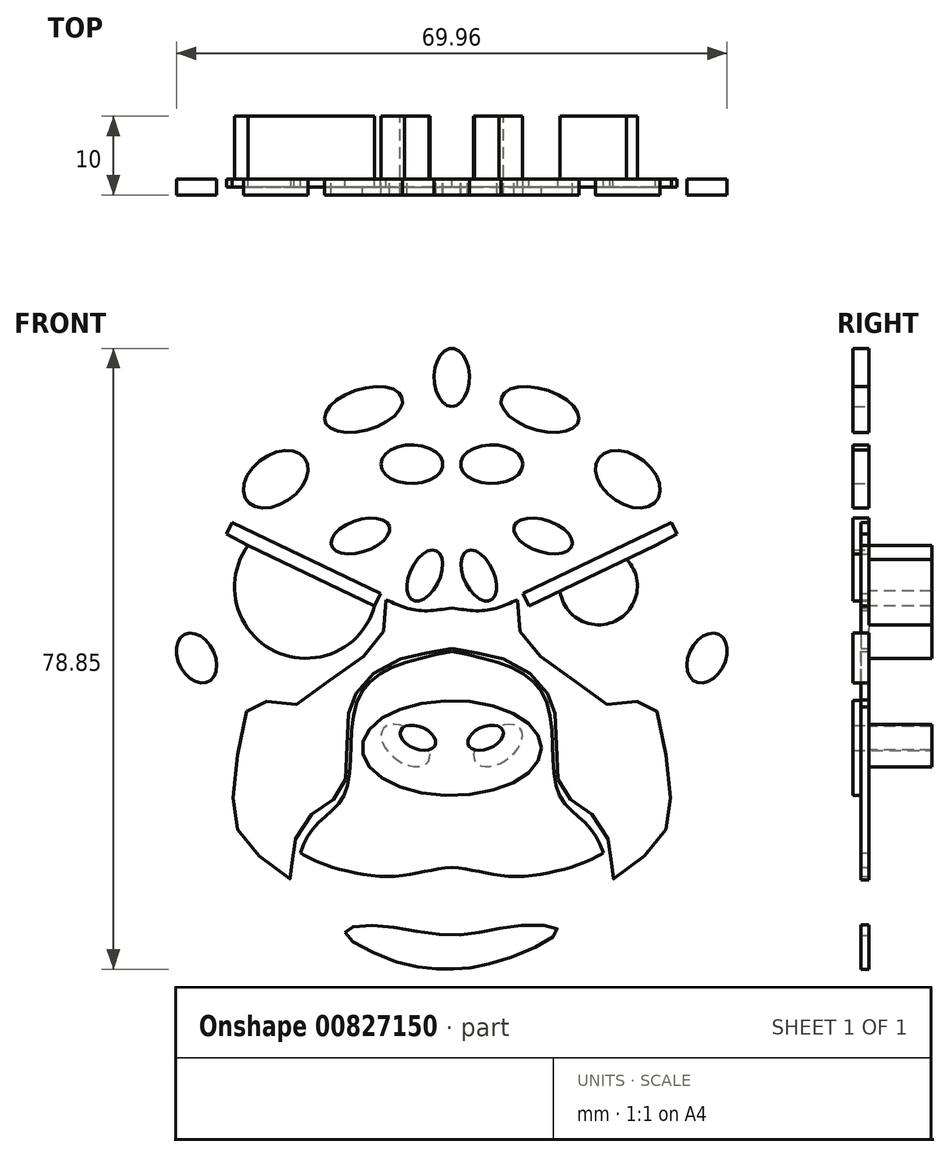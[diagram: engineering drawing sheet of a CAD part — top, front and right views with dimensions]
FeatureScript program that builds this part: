
annotation { "Feature Type Name" : "Feature", "Feature Type Description" : "" }
export const myFeature = defineFeature(function(context is Context, id is Id, definition is map)
    precondition{}
    {
        {
            var Q0;
            Q0=qCreatedBy(makeId("Front.planeOp"),FACE);
            var sketch = newSketch(context, id + "F0", { "sketchPlane" : qUnion([Q0])});
            skCircle(sketch, "E0", {"center": v(0, 0) * mm, "radius": 38.2 * mm});
            skArc(sketch, "E1", {"start": v(-19.43, -32.88) * mm, "mid": v(0, -44.73) * mm, "end": v(19.43, -32.88) * mm});
            skEllipticalArc(sketch, "E2", {});
            skEllipticalArc(sketch, "E3.MirrorCS", {});
            const initialGuessF0  = {"E2": [-0.024179114171380335, 0.029565248963423232, -0.3708058327198124, 0.9287104147262303, 0.016266278529680156, 0.009832884209598174, 4.81903926483246, 1.850120978367784], "E3.MirrorCS": [0.024179114171380335, 0.029565248963423232, 0.3708058327198124, 0.9287104147262303, 0.016266278529680156, 0.009832884209598174, 4.433064328811803, 1.4641460423471258]};
            skSetInitialGuess(sketch, initialGuessF0);
            skSolve(sketch);
        }
        {
            var Q0;
            Q0 = qSketchRegion(id + "F0", true);
            extrude(context, id + "F1", {"entities" : qUnion([Q0]), "depth" : 8 * mm, "offsetDistance" : 25.4 * mm});
        }
        {
            var Q0;
            Q0=makeQuery(id+"F1.opExtrude","CAP_FACE",FACE,{"disambiguationData":[OSD([sQuery(id+"F0.wireOp",EDGE,"E0")])],"isStart":false});
            var sketch = newSketch(context, id + "F2", { "sketchPlane" : qUnion([Q0])});
            skArc(sketch, "E4", {"start": v(9.8, 2.82) * mm, "mid": v(22.44, -2.93) * mm, "end": v(25.89, 10.53) * mm});
            skLineSegment(sketch, "E5", {"start": v(9.8, 2.82) * mm, "end": v(25.89, 10.53) * mm});
            skLineSegment(sketch, "E6.MirrorCS", {"start": v(-9.8, 2.82) * mm, "end": v(-25.89, 10.53) * mm});
            skArc(sketch, "E7.MirrorCS", {"start": v(-9.8, 2.82) * mm, "mid": v(-22.44, -2.93) * mm, "end": v(-25.89, 10.53) * mm});
            skEllipse(sketch, "E8", {"center": v(-5.88, -14.9) * mm, "majorRadius": 3.54 * mm, "minorRadius": 2.09 * mm, "majorAxis": v(-0.8, 0.6)});
            skEllipse(sketch, "E9.MirrorC", {"center": v(5.88, -14.9) * mm, "majorRadius": 3.54 * mm, "minorRadius": 2.09 * mm, "majorAxis": v(0.8, 0.6)});
            skEllipticalArc(sketch, "E10", {});
            skFitSpline(sketch, "E11", {"points": [v(-28.6, 24.5) * mm, v(-24.18, 29.57) * mm, v(-18.4, 32) * mm], "startDerivative": vector(7.89, 11.21) * mm, "endDerivative": vector(12.51, 3.7) * mm});
            skEllipticalArc(sketch, "E12.MirrorCS", {});
            skFitSpline(sketch, "E13.MirrorCS", {"points": [v(28.6, 24.5) * mm, v(24.18, 29.57) * mm, v(18.4, 32) * mm], "startDerivative": vector(-7.89, 11.21) * mm, "endDerivative": vector(-12.51, 3.7) * mm});
            skPoint(sketch, "E14.3.internal.snap0", {"position": v(-3.03, -17) * mm});
            skFitSpline(sketch, "E15", {"points": [v(-0.11, -33.34) * mm, v(-0.11, -33.34) * mm], "startDerivative": vector(0, 0) * mm, "endDerivative": vector(0, 0) * mm});
            skFitSpline(sketch, "E16", {"points": [v(-19.7, -29.84) * mm, v(-16.03, -34.27) * mm, v(-14.68, -37.12) * mm, v(-10.74, -36.92) * mm, v(-0.74, -37.72) * mm, v(0, -37.99) * mm], "startDerivative": vector(6.91, -19.77) * mm, "endDerivative": vector(6.14, -7.63) * mm});
            skFitSpline(sketch, "E17", {"points": [v(0.2, -33.51) * mm, v(-1.85, -33.51) * mm, v(-9.43, -32.38) * mm, v(-19.7, -29.84) * mm], "startDerivative": vector(-8.87, -1.04) * mm, "endDerivative": vector(-15.8, 10.96) * mm});
            skFitSpline(sketch, "E18.MirrorCS", {"points": [v(-0.2, -33.51) * mm, v(1.85, -33.51) * mm, v(9.43, -32.38) * mm, v(19.7, -29.84) * mm], "startDerivative": vector(8.87, -1.04) * mm, "endDerivative": vector(15.8, 10.96) * mm});
            skFitSpline(sketch, "E19.MirrorCS", {"points": [v(19.7, -29.84) * mm, v(16.03, -34.27) * mm, v(14.68, -37.12) * mm, v(10.74, -36.92) * mm, v(0.74, -37.72) * mm, v(0, -37.99) * mm], "startDerivative": vector(-6.91, -19.77) * mm, "endDerivative": vector(-6.14, -7.63) * mm});
            skArc(sketch, "E20", {"start": v(-22.21, 8.77) * mm, "mid": v(-20.78, 0.92) * mm, "end": v(-13.76, 4.72) * mm});
            skArc(sketch, "E21.MirrorCS", {"start": v(22.21, 8.77) * mm, "mid": v(20.78, 0.92) * mm, "end": v(13.76, 4.72) * mm});
            const initialGuessF2  = {"E10": [-0.024179114171380335, 0.029565248963423232, -0.3870836545444449, 0.9220445999974822, 0.010867715808404359, 0.006266824930289094, 4.71238898038469, 1.8461037695526126], "E12.MirrorCS": [0.024179114171380335, 0.029565248963423232, 0.3870836545444449, 0.9220445999974822, 0.010867715808404359, 0.006266824930289094, 4.437081537626973, 1.5707963267948966]};
            skSetInitialGuess(sketch, initialGuessF2);
            skSolve(sketch);
        }
        {
            var Q0;
            Q0=makeQuery(id+"F1.opExtrude","CAP_FACE",FACE,{"disambiguationData":[OSD([sQuery(id+"F0.wireOp",EDGE,"E0"),sQuery(id+"F0.wireOp",EDGE,"E1"),sQuery(id+"F0.wireOp",EDGE,"E2"),sQuery(id+"F0.wireOp",EDGE,"E3.MirrorCS")])],"isStart":false});
            var sketch = newSketch(context, id + "F3", { "sketchPlane" : qUnion([Q0])});
            skEllipse(sketch, "E22", {"center": v(-11.2, 27.78) * mm, "majorRadius": 5.12 * mm, "minorRadius": 2.63 * mm, "majorAxis": v(0.96, 0.3)});
            skEllipse(sketch, "E23", {"center": v(-5.07, 20.84) * mm, "majorRadius": 3.95 * mm, "minorRadius": 2.46 * mm, "majorAxis": v(-1, 0)});
            skEllipse(sketch, "E24", {"center": v(-22.35, 18.94) * mm, "majorRadius": 4.57 * mm, "minorRadius": 3.08 * mm, "majorAxis": v(0.8, 0.6)});
            skEllipse(sketch, "E25", {"center": v(-11.6, 11.73) * mm, "majorRadius": 3.87 * mm, "minorRadius": 2.02 * mm, "majorAxis": v(0.95, 0.32)});
            skEllipse(sketch, "E26", {"center": v(-3.44, 6.7) * mm, "majorRadius": 3.47 * mm, "minorRadius": 1.9 * mm, "majorAxis": v(0.43, 0.9)});
            skEllipse(sketch, "E27", {"center": v(0, 31.87) * mm, "majorRadius": 3.67 * mm, "minorRadius": 2.24 * mm, "majorAxis": v(0, -1)});
            skEllipse(sketch, "E28", {"center": v(-32.42, -3.79) * mm, "majorRadius": 3.35 * mm, "minorRadius": 2.32 * mm, "majorAxis": v(-0.45, 0.9)});
            skEllipse(sketch, "E29", {"center": v(0, -15.22) * mm, "majorRadius": 11.4 * mm, "minorRadius": 6.02 * mm, "majorAxis": v(1, 0)});
            skEllipse(sketch, "E30.MirrorC", {"center": v(3.44, 6.7) * mm, "majorRadius": 3.47 * mm, "minorRadius": 1.9 * mm, "majorAxis": v(-0.43, 0.9)});
            skEllipse(sketch, "E31.MirrorC", {"center": v(11.6, 11.73) * mm, "majorRadius": 3.87 * mm, "minorRadius": 2.02 * mm, "majorAxis": v(-0.95, 0.32)});
            skEllipse(sketch, "E32.MirrorC", {"center": v(22.35, 18.94) * mm, "majorRadius": 4.57 * mm, "minorRadius": 3.08 * mm, "majorAxis": v(-0.8, 0.6)});
            skEllipse(sketch, "E33.MirrorC", {"center": v(11.2, 27.78) * mm, "majorRadius": 5.12 * mm, "minorRadius": 2.63 * mm, "majorAxis": v(-0.96, 0.3)});
            skEllipse(sketch, "E34.MirrorC", {"center": v(5.07, 20.84) * mm, "majorRadius": 3.95 * mm, "minorRadius": 2.46 * mm, "majorAxis": v(1, 0)});
            skEllipse(sketch, "E35.MirrorC", {"center": v(32.42, -3.79) * mm, "majorRadius": 3.35 * mm, "minorRadius": 2.32 * mm, "majorAxis": v(0.45, 0.9)});
            skSolve(sketch);
        }
        {
            var Q0;
            Q0 = qSketchRegion(id + "F3", true);
            extrude(context, id + "F4", {"entities" : qUnion([Q0]), "operationType" : NewBodyOperationType.ADD, "depth" : 2 * mm, "offsetDistance" : 25.4 * mm});
        }
        {
            var Q0;
            {var subQ0=sQuery(id+"F2.wireOp",EDGE,"E7.MirrorCS");Q0=makeQuery(id+"F2.imprint","IMPRINT",FACE,{"disambiguationData":[TD([[makeQuery(id+"F2.imprint","IMPRINT",EDGE,{"derivedFrom":subQ0}),-1.0]])]});}
            var Q1;
            {var subQ0=sQuery(id+"F2.wireOp",EDGE,"E4");Q1=makeQuery(id+"F2.imprint","IMPRINT",FACE,{"disambiguationData":[TD([[makeQuery(id+"F2.imprint","IMPRINT",EDGE,{"derivedFrom":subQ0}),1.0]])]});}
            var Q2;
            {var subQ0=sQuery(id+"F2.wireOp",EDGE,"E16");Q2=makeQuery(id+"F2.imprint","IMPRINT",FACE,{"disambiguationData":[TD([[makeQuery(id+"F2.imprint","IMPRINT",EDGE,{"derivedFrom":subQ0}),1.0]])]});}
            var Q3;
            Q3=makeQuery(id+"F2.imprint","IMPRINT",FACE,{"disambiguationData":[TD([[makeQuery(id+"F2.imprint","IMPRINT",EDGE,{"derivedFrom":sQuery(id+"F2.wireOp",EDGE,"E10")}),1.0]])]});
            var Q4;
            Q4=makeQuery(id+"F2.imprint","IMPRINT",FACE,{"disambiguationData":[TD([[makeQuery(id+"F2.imprint","IMPRINT",EDGE,{"derivedFrom":sQuery(id+"F2.wireOp",EDGE,"E12.MirrorCS")}),1.0]])]});
            extrude(context, id + "F5", {"entities" : qUnion([Q0, Q1, Q2, Q3, Q4]), "operationType" : NewBodyOperationType.REMOVE, "oppositeDirection" : true, "depth" : 25.4 * mm, "offsetDistance" : 25.4 * mm});
        }
        {
            var Q0;
            Q0=makeQuery(id+"F1.opExtrude","CAP_FACE",FACE,{"disambiguationData":[OSD([sQuery(id+"F0.wireOp",EDGE,"E0"),sQuery(id+"F0.wireOp",EDGE,"E1"),sQuery(id+"F0.wireOp",EDGE,"E2"),sQuery(id+"F0.wireOp",EDGE,"E3.MirrorCS")])],"isStart":false});
            var sketch = newSketch(context, id + "F6", { "sketchPlane" : qUnion([Q0])});
            skLineSegment(sketch, "E36", {"start": v(-9.8, 2.82) * mm, "end": v(-9.03, 4.41) * mm});
            skLineSegment(sketch, "E37", {"start": v(-9.03, 4.41) * mm, "end": v(-27.9, 13.46) * mm});
            skLineSegment(sketch, "E38", {"start": v(-27.9, 13.46) * mm, "end": v(-28.62, 11.98) * mm});
            skLineSegment(sketch, "E39", {"start": v(-28.62, 11.98) * mm, "end": v(-25.89, 10.53) * mm});
            skLineSegment(sketch, "E40", {"start": v(-25.89, 10.53) * mm, "end": v(-13.76, 4.72) * mm});
            skLineSegment(sketch, "E41.MirrorCS", {"start": v(25.89, 10.53) * mm, "end": v(13.76, 4.72) * mm});
            skLineSegment(sketch, "E42.MirrorCS", {"start": v(9.03, 4.41) * mm, "end": v(27.9, 13.46) * mm});
            skLineSegment(sketch, "E43.MirrorCS", {"start": v(27.9, 13.46) * mm, "end": v(28.62, 11.98) * mm});
            skLineSegment(sketch, "E44.MirrorCS", {"start": v(28.62, 11.98) * mm, "end": v(25.89, 10.53) * mm});
            skLineSegment(sketch, "E45.MirrorCS", {"start": v(9.8, 2.82) * mm, "end": v(9.03, 4.41) * mm});
            skFitSpline(sketch, "E46", {"points": [v(0, -2.92) * mm, v(-11.67, -8.46) * mm, v(-13.44, -20.65) * mm, v(-17.28, -25.03) * mm, v(-19.7, -29.84) * mm], "startDerivative": vector(-49.21, -10.04) * mm, "endDerivative": vector(-9.35, -27.58) * mm});
            skLineSegment(sketch, "E47", {"start": v(-13.76, 4.72) * mm, "end": v(-9.8, 2.82) * mm});
            skLineSegment(sketch, "E48", {"start": v(13.76, 4.72) * mm, "end": v(9.8, 2.82) * mm});
            skFitSpline(sketch, "E49.MirrorCS", {"points": [v(0, -2.92) * mm, v(11.67, -8.46) * mm, v(13.44, -20.65) * mm, v(17.28, -25.03) * mm, v(19.7, -29.84) * mm], "startDerivative": vector(49.21, -10.04) * mm, "endDerivative": vector(9.35, -27.58) * mm});
            skFitSpline(sketch, "E50", {"points": [v(-19.24, -28.54) * mm, v(-16.35, -29.94) * mm, v(-7.65, -31.52) * mm, v(0, -30.38) * mm, v(7.99, -31) * mm, v(19.24, -28.54) * mm], "startDerivative": vector(18.38, -10.57) * mm, "endDerivative": vector(47.4, 14.65) * mm});
            skPoint(sketch, "E51.orphan", {"position": v(0, -26.44) * mm});
            skFitSpline(sketch, "E52.MirrorCS", {"points": [v(19.24, -28.54) * mm, v(16.35, -29.94) * mm, v(7.65, -31.52) * mm, v(0, -30.38) * mm, v(-7.99, -31) * mm, v(-19.24, -28.54) * mm], "startDerivative": vector(-18.38, -10.57) * mm, "endDerivative": vector(-47.4, 14.65) * mm});
            skSolve(sketch);
        }
        {
            var Q0;
            Q0 = qSketchRegion(id + "F6", true);
            extrude(context, id + "F7", {"entities" : qUnion([Q0]), "operationType" : NewBodyOperationType.ADD, "depth" : 1 * mm, "offsetDistance" : 25.4 * mm});
        }
        {
            var Q0;
            Q0=makeQuery(id+"F4.opExtrude","CAP_FACE",FACE,{"disambiguationData":[OSD([sQuery(id+"F3.wireOp",EDGE,"E29")])],"isStart":false});
            var sketch = newSketch(context, id + "F8", { "sketchPlane" : qUnion([Q0])});
            skEllipse(sketch, "E53", {"center": v(-4.28, -13.91) * mm, "majorRadius": 2.39 * mm, "minorRadius": 1.41 * mm, "majorAxis": v(-0.92, 0.4)});
            skEllipse(sketch, "E54.MirrorC", {"center": v(4.28, -13.91) * mm, "majorRadius": 2.39 * mm, "minorRadius": 1.41 * mm, "majorAxis": v(0.92, 0.4)});
            skSolve(sketch);
        }
        {
            var Q0;
            Q0 = qSketchRegion(id + "F8", true);
            extrude(context, id + "F9", {"entities" : qUnion([Q0]), "operationType" : NewBodyOperationType.REMOVE, "oppositeDirection" : true, "depth" : 25.4 * mm, "offsetDistance" : 25.4 * mm});
        }
        {
            var Q0;
            {var subQ0=sQuery(id+"F2.wireOp",EDGE,"E7.MirrorCS");var subQ1=sQuery(id+"F2.wireOp",EDGE,"E6.MirrorCS");var subQ3=sQuery(id+"F0.wireOp",EDGE,"E3.MirrorCS");var subQ4=sQuery(id+"F0.wireOp",EDGE,"E2");var subQ5=sQuery(id+"F2.wireOp",EDGE,"E5");var subQ6=sQuery(id+"F2.wireOp",EDGE,"E4");var subQ8=sQuery(id+"F0.wireOp",EDGE,"E1");var subQ9=sQuery(id+"F0.wireOp",EDGE,"E0");var subQ10=makeQuery(id+"F1.opExtrude","CAP_FACE",FACE,{"disambiguationData":[OSD([subQ9,subQ8,subQ4,subQ3])],"isStart":false});Q0=makeQuery(id+"F7.boolean.opBoolean","SPLIT",FACE,{"disambiguationData":[TD([makeQuery(id+"F1.opExtrude","SWEPT_FACE",FACE,{"disambiguationData":[OSD([subQ9]),TDD([makeQuery(id+"F0.imprint","IMPRINT",EDGE,{"disambiguationData":[TD([[makeQuery(id+"F0.imprint","INTERSECT",VERTEX,{"disambiguationData":[OD(0.0)],"derivedFrom":[subQ9,subQ4]}),1.0]])],"derivedFrom":subQ9})])]}),subQ10,makeQuery(id+"F1.opExtrude","SWEPT_FACE",FACE,{"disambiguationData":[OSD([subQ9]),TDD([makeQuery(id+"F0.imprint","IMPRINT",EDGE,{"disambiguationData":[TD([[makeQuery(id+"F0.imprint","INTERSECT",VERTEX,{"disambiguationData":[OD(0.0)],"derivedFrom":[subQ9,subQ8]}),1.0]])],"derivedFrom":subQ9})])]}),makeQuery(id+"F1.opExtrude","SWEPT_FACE",FACE,{"disambiguationData":[OSD([subQ9]),TDD([makeQuery(id+"F0.imprint","IMPRINT",EDGE,{"disambiguationData":[TD([[makeQuery(id+"F0.imprint","INTERSECT",VERTEX,{"disambiguationData":[OD(1.0)],"derivedFrom":[subQ9,subQ8]}),-1.0]])],"derivedFrom":subQ9})])]}),makeQuery(id+"F1.opExtrude","SWEPT_FACE",FACE,{"disambiguationData":[OSD([subQ8])]}),makeQuery(id+"F1.opExtrude","SWEPT_FACE",FACE,{"disambiguationData":[OSD([subQ4])]}),makeQuery(id+"F1.opExtrude","SWEPT_FACE",FACE,{"disambiguationData":[OSD([subQ3])]}),makeQuery(id+"F4.opExtrude","SWEPT_FACE",FACE,{"disambiguationData":[OSD([sQuery(id+"F3.wireOp",EDGE,"E22")])]}),makeQuery(id+"F4.opExtrude","SWEPT_FACE",FACE,{"disambiguationData":[OSD([sQuery(id+"F3.wireOp",EDGE,"E23")])]}),makeQuery(id+"F4.opExtrude","SWEPT_FACE",FACE,{"disambiguationData":[OSD([sQuery(id+"F3.wireOp",EDGE,"E24")])]}),makeQuery(id+"F4.opExtrude","SWEPT_FACE",FACE,{"disambiguationData":[OSD([sQuery(id+"F3.wireOp",EDGE,"E25")])]}),makeQuery(id+"F4.opExtrude","SWEPT_FACE",FACE,{"disambiguationData":[OSD([sQuery(id+"F3.wireOp",EDGE,"E26")])]}),makeQuery(id+"F4.opExtrude","SWEPT_FACE",FACE,{"disambiguationData":[OSD([sQuery(id+"F3.wireOp",EDGE,"E27")])]}),makeQuery(id+"F4.opExtrude","SWEPT_FACE",FACE,{"disambiguationData":[OSD([sQuery(id+"F3.wireOp",EDGE,"E28")])]}),makeQuery(id+"F4.opExtrude","SWEPT_FACE",FACE,{"disambiguationData":[OSD([sQuery(id+"F3.wireOp",EDGE,"E30.MirrorC")])]}),makeQuery(id+"F4.opExtrude","SWEPT_FACE",FACE,{"disambiguationData":[OSD([sQuery(id+"F3.wireOp",EDGE,"E31.MirrorC")])]}),makeQuery(id+"F4.opExtrude","SWEPT_FACE",FACE,{"disambiguationData":[OSD([sQuery(id+"F3.wireOp",EDGE,"E32.MirrorC")])]}),makeQuery(id+"F4.opExtrude","SWEPT_FACE",FACE,{"disambiguationData":[OSD([sQuery(id+"F3.wireOp",EDGE,"E33.MirrorC")])]}),makeQuery(id+"F4.opExtrude","SWEPT_FACE",FACE,{"disambiguationData":[OSD([sQuery(id+"F3.wireOp",EDGE,"E34.MirrorC")])]}),makeQuery(id+"F4.opExtrude","SWEPT_FACE",FACE,{"disambiguationData":[OSD([sQuery(id+"F3.wireOp",EDGE,"E35.MirrorC")])]}),makeQuery(id+"F5.boolean.opBoolean","COPY",FACE,{"derivedFrom":makeQuery(id+"F5.opExtrude","SWEPT_FACE",FACE,{"disambiguationData":[OSD([subQ6])]})}),makeQuery(id+"F5.boolean.opBoolean","COPY",FACE,{"derivedFrom":makeQuery(id+"F5.opExtrude","SWEPT_FACE",FACE,{"disambiguationData":[OSD([subQ5]),TDD([makeQuery(id+"F2.imprint","IMPRINT",EDGE,{"disambiguationData":[TD([[makeQuery(id+"F2.imprint","INTERSECT",VERTEX,{"disambiguationData":[OD(0.0)],"derivedFrom":[subQ6,subQ5]}),-1.0]])],"derivedFrom":subQ5})])]})}),makeQuery(id+"F5.boolean.opBoolean","COPY",FACE,{"derivedFrom":makeQuery(id+"F5.opExtrude","SWEPT_FACE",FACE,{"disambiguationData":[OSD([subQ5]),TDD([makeQuery(id+"F2.imprint","IMPRINT",EDGE,{"disambiguationData":[TD([[makeQuery(id+"F2.imprint","INTERSECT",VERTEX,{"disambiguationData":[OD(1.0)],"derivedFrom":[subQ6,subQ5]}),1.0]])],"derivedFrom":subQ5})])]})}),makeQuery(id+"F5.boolean.opBoolean","COPY",FACE,{"derivedFrom":makeQuery(id+"F5.opExtrude","SWEPT_FACE",FACE,{"disambiguationData":[OSD([subQ1]),TDD([makeQuery(id+"F2.imprint","IMPRINT",EDGE,{"disambiguationData":[TD([[makeQuery(id+"F2.imprint","INTERSECT",VERTEX,{"disambiguationData":[OD(0.0)],"derivedFrom":[subQ1,subQ0]}),-1.0]])],"derivedFrom":subQ1})])]})}),makeQuery(id+"F5.boolean.opBoolean","COPY",FACE,{"derivedFrom":makeQuery(id+"F5.opExtrude","SWEPT_FACE",FACE,{"disambiguationData":[OSD([subQ1]),TDD([makeQuery(id+"F2.imprint","IMPRINT",EDGE,{"disambiguationData":[TD([[makeQuery(id+"F2.imprint","INTERSECT",VERTEX,{"disambiguationData":[OD(1.0)],"derivedFrom":[subQ1,subQ0]}),1.0]])],"derivedFrom":subQ1})])]})}),makeQuery(id+"F5.boolean.opBoolean","COPY",FACE,{"derivedFrom":makeQuery(id+"F5.opExtrude","SWEPT_FACE",FACE,{"disambiguationData":[OSD([subQ0])]})}),makeQuery(id+"F5.boolean.opBoolean","COPY",FACE,{"derivedFrom":makeQuery(id+"F5.opExtrude","SWEPT_FACE",FACE,{"disambiguationData":[OSD([sQuery(id+"F2.wireOp",EDGE,"E10")])]})}),makeQuery(id+"F5.boolean.opBoolean","COPY",FACE,{"derivedFrom":makeQuery(id+"F5.opExtrude","SWEPT_FACE",FACE,{"disambiguationData":[OSD([sQuery(id+"F2.wireOp",EDGE,"E11")])]})}),makeQuery(id+"F5.boolean.opBoolean","COPY",FACE,{"derivedFrom":makeQuery(id+"F5.opExtrude","SWEPT_FACE",FACE,{"disambiguationData":[OSD([sQuery(id+"F2.wireOp",EDGE,"E12.MirrorCS")])]})}),makeQuery(id+"F5.boolean.opBoolean","COPY",FACE,{"derivedFrom":makeQuery(id+"F5.opExtrude","SWEPT_FACE",FACE,{"disambiguationData":[OSD([sQuery(id+"F2.wireOp",EDGE,"E13.MirrorCS")])]})}),makeQuery(id+"F5.boolean.opBoolean","COPY",FACE,{"derivedFrom":makeQuery(id+"F5.opExtrude","SWEPT_FACE",FACE,{"disambiguationData":[OSD([sQuery(id+"F2.wireOp",EDGE,"E16")])]})}),makeQuery(id+"F5.boolean.opBoolean","COPY",FACE,{"derivedFrom":makeQuery(id+"F5.opExtrude","SWEPT_FACE",FACE,{"disambiguationData":[OSD([sQuery(id+"F2.wireOp",EDGE,"E17")])]})}),makeQuery(id+"F5.boolean.opBoolean","COPY",FACE,{"derivedFrom":makeQuery(id+"F5.opExtrude","SWEPT_FACE",FACE,{"disambiguationData":[OSD([sQuery(id+"F2.wireOp",EDGE,"E18.MirrorCS")])]})}),makeQuery(id+"F5.boolean.opBoolean","COPY",FACE,{"derivedFrom":makeQuery(id+"F5.opExtrude","SWEPT_FACE",FACE,{"disambiguationData":[OSD([sQuery(id+"F2.wireOp",EDGE,"E19.MirrorCS")])]})}),makeQuery(id+"F7.opExtrude","SWEPT_FACE",FACE,{"disambiguationData":[OSD([sQuery(id+"F6.wireOp",EDGE,"E36")])]}),makeQuery(id+"F7.opExtrude","SWEPT_FACE",FACE,{"disambiguationData":[OSD([sQuery(id+"F6.wireOp",EDGE,"E37")])]}),makeQuery(id+"F7.opExtrude","SWEPT_FACE",FACE,{"disambiguationData":[OSD([sQuery(id+"F6.wireOp",EDGE,"E38")])]}),makeQuery(id+"F7.opExtrude","SWEPT_FACE",FACE,{"disambiguationData":[OSD([sQuery(id+"F6.wireOp",EDGE,"E39")])]}),makeQuery(id+"F7.opExtrude","SWEPT_FACE",FACE,{"disambiguationData":[OSD([sQuery(id+"F6.wireOp",EDGE,"E40"),sQuery(id+"F6.wireOp",EDGE,"E47")])]}),makeQuery(id+"F7.opExtrude","SWEPT_FACE",FACE,{"disambiguationData":[OSD([sQuery(id+"F6.wireOp",EDGE,"E41.MirrorCS"),sQuery(id+"F6.wireOp",EDGE,"E48")])]}),makeQuery(id+"F7.opExtrude","SWEPT_FACE",FACE,{"disambiguationData":[OSD([sQuery(id+"F6.wireOp",EDGE,"E42.MirrorCS")])]}),makeQuery(id+"F7.opExtrude","SWEPT_FACE",FACE,{"disambiguationData":[OSD([sQuery(id+"F6.wireOp",EDGE,"E43.MirrorCS")])]}),makeQuery(id+"F7.opExtrude","SWEPT_FACE",FACE,{"disambiguationData":[OSD([sQuery(id+"F6.wireOp",EDGE,"E44.MirrorCS")])]}),makeQuery(id+"F7.opExtrude","SWEPT_FACE",FACE,{"disambiguationData":[OSD([sQuery(id+"F6.wireOp",EDGE,"E45.MirrorCS")])]}),makeQuery(id+"F7.opExtrude","SWEPT_FACE",FACE,{"disambiguationData":[OSD([sQuery(id+"F6.wireOp",EDGE,"E46")])]}),makeQuery(id+"F7.opExtrude","SWEPT_FACE",FACE,{"disambiguationData":[OSD([sQuery(id+"F6.wireOp",EDGE,"020a8742-f3d3-43aa-8d11-e984b5552f450.MirrorCS")])]}),makeQuery(id+"F7.opExtrude","SWEPT_FACE",FACE,{"disambiguationData":[OSD([sQuery(id+"F6.wireOp",EDGE,"7f19501d-313e-40a1-b078-9e00cbc5491b")])]})])],"derivedFrom":subQ10});}
            var sketch = newSketch(context, id + "F10", { "sketchPlane" : qUnion([Q0])});
            skPoint(sketch, "E55.0.internal.snap0", {"position": v(-9.41, 3.61) * mm});
            skFitSpline(sketch, "E55", {"points": [v(-8.33, 3.61) * mm, v(-9.03, -1.34) * mm, v(-14.5, -5.83) * mm, v(-21.07, -9.97) * mm, v(-24.99, -9.16) * mm, v(-27.19, -15.97) * mm, v(-27.63, -24.14) * mm, v(-25, -28.4) * mm, v(-20.1, -31.96) * mm, v(-20.35, -30.3) * mm, v(-19.7, -26.34) * mm, v(-17.04, -22.96) * mm, v(-14.37, -21.14) * mm, v(-13.36, -17.9) * mm, v(-13.19, -11.6) * mm, v(-12.57, -9.15) * mm, v(-10.95, -6.65) * mm, v(-7.04, -4.1) * mm, v(-3.39, -3.18) * mm, v(0, -2.56) * mm], "startDerivative": vector(-1.81, -87.44) * mm, "endDerivative": vector(73.72, 13.54) * mm});
            skFitSpline(sketch, "E56", {"points": [v(-8.33, 3.61) * mm, v(-4.45, 2.3) * mm, v(0, 2.59) * mm], "startDerivative": vector(7.74, -3.5) * mm, "endDerivative": vector(8.92, 1.42) * mm});
            skFitSpline(sketch, "E57.MirrorCS", {"points": [v(8.33, 3.61) * mm, v(4.45, 2.3) * mm, v(0, 2.59) * mm], "startDerivative": vector(-7.74, -3.5) * mm, "endDerivative": vector(-8.92, 1.42) * mm});
            skFitSpline(sketch, "E58.MirrorCS", {"points": [v(8.33, 3.61) * mm, v(9.03, -1.34) * mm, v(14.5, -5.83) * mm, v(21.07, -9.97) * mm, v(24.99, -9.16) * mm, v(27.19, -15.97) * mm, v(27.63, -24.14) * mm, v(25, -28.4) * mm, v(20.1, -31.96) * mm, v(20.35, -30.3) * mm, v(19.7, -26.34) * mm, v(17.04, -22.96) * mm, v(14.37, -21.14) * mm, v(13.36, -17.9) * mm, v(13.19, -11.6) * mm, v(12.57, -9.15) * mm, v(10.95, -6.65) * mm, v(7.04, -4.1) * mm, v(3.39, -3.18) * mm, v(0, -2.56) * mm], "startDerivative": vector(1.81, -87.44) * mm, "endDerivative": vector(-73.72, 13.54) * mm});
            skSolve(sketch);
        }
        {
            var Q0;
            Q0 = qSketchRegion(id + "F10", true);
            extrude(context, id + "F11", {"entities" : qUnion([Q0]), "operationType" : NewBodyOperationType.ADD, "depth" : 1 * mm, "offsetDistance" : 25.4 * mm});
        }
        {
            var Q0;
            {var subQ0=sQuery(id+"F2.wireOp",EDGE,"E7.MirrorCS");var subQ1=sQuery(id+"F2.wireOp",EDGE,"E6.MirrorCS");var subQ3=sQuery(id+"F0.wireOp",EDGE,"E3.MirrorCS");var subQ4=sQuery(id+"F0.wireOp",EDGE,"E2");var subQ5=sQuery(id+"F2.wireOp",EDGE,"E5");var subQ6=sQuery(id+"F2.wireOp",EDGE,"E4");var subQ8=sQuery(id+"F0.wireOp",EDGE,"E1");var subQ9=sQuery(id+"F0.wireOp",EDGE,"E0");var subQ10=makeQuery(id+"F1.opExtrude","CAP_FACE",FACE,{"disambiguationData":[OSD([subQ9,subQ8,subQ4,subQ3])],"isStart":false});Q0=makeQuery(id+"F7.boolean.opBoolean","SPLIT",FACE,{"disambiguationData":[TD([makeQuery(id+"F1.opExtrude","SWEPT_FACE",FACE,{"disambiguationData":[OSD([subQ9]),TDD([makeQuery(id+"F0.imprint","IMPRINT",EDGE,{"disambiguationData":[TD([[makeQuery(id+"F0.imprint","INTERSECT",VERTEX,{"disambiguationData":[OD(0.0)],"derivedFrom":[subQ9,subQ4]}),1.0]])],"derivedFrom":subQ9})])]}),subQ10,makeQuery(id+"F1.opExtrude","SWEPT_FACE",FACE,{"disambiguationData":[OSD([subQ9]),TDD([makeQuery(id+"F0.imprint","IMPRINT",EDGE,{"disambiguationData":[TD([[makeQuery(id+"F0.imprint","INTERSECT",VERTEX,{"disambiguationData":[OD(0.0)],"derivedFrom":[subQ9,subQ8]}),1.0]])],"derivedFrom":subQ9})])]}),makeQuery(id+"F1.opExtrude","SWEPT_FACE",FACE,{"disambiguationData":[OSD([subQ9]),TDD([makeQuery(id+"F0.imprint","IMPRINT",EDGE,{"disambiguationData":[TD([[makeQuery(id+"F0.imprint","INTERSECT",VERTEX,{"disambiguationData":[OD(1.0)],"derivedFrom":[subQ9,subQ8]}),-1.0]])],"derivedFrom":subQ9})])]}),makeQuery(id+"F1.opExtrude","SWEPT_FACE",FACE,{"disambiguationData":[OSD([subQ8])]}),makeQuery(id+"F1.opExtrude","SWEPT_FACE",FACE,{"disambiguationData":[OSD([subQ4])]}),makeQuery(id+"F1.opExtrude","SWEPT_FACE",FACE,{"disambiguationData":[OSD([subQ3])]}),makeQuery(id+"F4.opExtrude","SWEPT_FACE",FACE,{"disambiguationData":[OSD([sQuery(id+"F3.wireOp",EDGE,"E22")])]}),makeQuery(id+"F4.opExtrude","SWEPT_FACE",FACE,{"disambiguationData":[OSD([sQuery(id+"F3.wireOp",EDGE,"E23")])]}),makeQuery(id+"F4.opExtrude","SWEPT_FACE",FACE,{"disambiguationData":[OSD([sQuery(id+"F3.wireOp",EDGE,"E24")])]}),makeQuery(id+"F4.opExtrude","SWEPT_FACE",FACE,{"disambiguationData":[OSD([sQuery(id+"F3.wireOp",EDGE,"E25")])]}),makeQuery(id+"F4.opExtrude","SWEPT_FACE",FACE,{"disambiguationData":[OSD([sQuery(id+"F3.wireOp",EDGE,"E26")])]}),makeQuery(id+"F4.opExtrude","SWEPT_FACE",FACE,{"disambiguationData":[OSD([sQuery(id+"F3.wireOp",EDGE,"E27")])]}),makeQuery(id+"F4.opExtrude","SWEPT_FACE",FACE,{"disambiguationData":[OSD([sQuery(id+"F3.wireOp",EDGE,"E28")])]}),makeQuery(id+"F4.opExtrude","SWEPT_FACE",FACE,{"disambiguationData":[OSD([sQuery(id+"F3.wireOp",EDGE,"E30.MirrorC")])]}),makeQuery(id+"F4.opExtrude","SWEPT_FACE",FACE,{"disambiguationData":[OSD([sQuery(id+"F3.wireOp",EDGE,"E31.MirrorC")])]}),makeQuery(id+"F4.opExtrude","SWEPT_FACE",FACE,{"disambiguationData":[OSD([sQuery(id+"F3.wireOp",EDGE,"E32.MirrorC")])]}),makeQuery(id+"F4.opExtrude","SWEPT_FACE",FACE,{"disambiguationData":[OSD([sQuery(id+"F3.wireOp",EDGE,"E33.MirrorC")])]}),makeQuery(id+"F4.opExtrude","SWEPT_FACE",FACE,{"disambiguationData":[OSD([sQuery(id+"F3.wireOp",EDGE,"E34.MirrorC")])]}),makeQuery(id+"F4.opExtrude","SWEPT_FACE",FACE,{"disambiguationData":[OSD([sQuery(id+"F3.wireOp",EDGE,"E35.MirrorC")])]}),makeQuery(id+"F5.boolean.opBoolean","COPY",FACE,{"derivedFrom":makeQuery(id+"F5.opExtrude","SWEPT_FACE",FACE,{"disambiguationData":[OSD([subQ6])]})}),makeQuery(id+"F5.boolean.opBoolean","COPY",FACE,{"derivedFrom":makeQuery(id+"F5.opExtrude","SWEPT_FACE",FACE,{"disambiguationData":[OSD([subQ5]),TDD([makeQuery(id+"F2.imprint","IMPRINT",EDGE,{"disambiguationData":[TD([[makeQuery(id+"F2.imprint","INTERSECT",VERTEX,{"disambiguationData":[OD(0.0)],"derivedFrom":[subQ6,subQ5]}),-1.0]])],"derivedFrom":subQ5})])]})}),makeQuery(id+"F5.boolean.opBoolean","COPY",FACE,{"derivedFrom":makeQuery(id+"F5.opExtrude","SWEPT_FACE",FACE,{"disambiguationData":[OSD([subQ5]),TDD([makeQuery(id+"F2.imprint","IMPRINT",EDGE,{"disambiguationData":[TD([[makeQuery(id+"F2.imprint","INTERSECT",VERTEX,{"disambiguationData":[OD(1.0)],"derivedFrom":[subQ6,subQ5]}),1.0]])],"derivedFrom":subQ5})])]})}),makeQuery(id+"F5.boolean.opBoolean","COPY",FACE,{"derivedFrom":makeQuery(id+"F5.opExtrude","SWEPT_FACE",FACE,{"disambiguationData":[OSD([subQ1]),TDD([makeQuery(id+"F2.imprint","IMPRINT",EDGE,{"disambiguationData":[TD([[makeQuery(id+"F2.imprint","INTERSECT",VERTEX,{"disambiguationData":[OD(0.0)],"derivedFrom":[subQ1,subQ0]}),-1.0]])],"derivedFrom":subQ1})])]})}),makeQuery(id+"F5.boolean.opBoolean","COPY",FACE,{"derivedFrom":makeQuery(id+"F5.opExtrude","SWEPT_FACE",FACE,{"disambiguationData":[OSD([subQ1]),TDD([makeQuery(id+"F2.imprint","IMPRINT",EDGE,{"disambiguationData":[TD([[makeQuery(id+"F2.imprint","INTERSECT",VERTEX,{"disambiguationData":[OD(1.0)],"derivedFrom":[subQ1,subQ0]}),1.0]])],"derivedFrom":subQ1})])]})}),makeQuery(id+"F5.boolean.opBoolean","COPY",FACE,{"derivedFrom":makeQuery(id+"F5.opExtrude","SWEPT_FACE",FACE,{"disambiguationData":[OSD([subQ0])]})}),makeQuery(id+"F5.boolean.opBoolean","COPY",FACE,{"derivedFrom":makeQuery(id+"F5.opExtrude","SWEPT_FACE",FACE,{"disambiguationData":[OSD([sQuery(id+"F2.wireOp",EDGE,"E10")])]})}),makeQuery(id+"F5.boolean.opBoolean","COPY",FACE,{"derivedFrom":makeQuery(id+"F5.opExtrude","SWEPT_FACE",FACE,{"disambiguationData":[OSD([sQuery(id+"F2.wireOp",EDGE,"E11")])]})}),makeQuery(id+"F5.boolean.opBoolean","COPY",FACE,{"derivedFrom":makeQuery(id+"F5.opExtrude","SWEPT_FACE",FACE,{"disambiguationData":[OSD([sQuery(id+"F2.wireOp",EDGE,"E12.MirrorCS")])]})}),makeQuery(id+"F5.boolean.opBoolean","COPY",FACE,{"derivedFrom":makeQuery(id+"F5.opExtrude","SWEPT_FACE",FACE,{"disambiguationData":[OSD([sQuery(id+"F2.wireOp",EDGE,"E13.MirrorCS")])]})}),makeQuery(id+"F5.boolean.opBoolean","COPY",FACE,{"derivedFrom":makeQuery(id+"F5.opExtrude","SWEPT_FACE",FACE,{"disambiguationData":[OSD([sQuery(id+"F2.wireOp",EDGE,"E16")])]})}),makeQuery(id+"F5.boolean.opBoolean","COPY",FACE,{"derivedFrom":makeQuery(id+"F5.opExtrude","SWEPT_FACE",FACE,{"disambiguationData":[OSD([sQuery(id+"F2.wireOp",EDGE,"E17")])]})}),makeQuery(id+"F5.boolean.opBoolean","COPY",FACE,{"derivedFrom":makeQuery(id+"F5.opExtrude","SWEPT_FACE",FACE,{"disambiguationData":[OSD([sQuery(id+"F2.wireOp",EDGE,"E18.MirrorCS")])]})}),makeQuery(id+"F5.boolean.opBoolean","COPY",FACE,{"derivedFrom":makeQuery(id+"F5.opExtrude","SWEPT_FACE",FACE,{"disambiguationData":[OSD([sQuery(id+"F2.wireOp",EDGE,"E19.MirrorCS")])]})}),makeQuery(id+"F7.opExtrude","SWEPT_FACE",FACE,{"disambiguationData":[OSD([sQuery(id+"F6.wireOp",EDGE,"E36")])]}),makeQuery(id+"F7.opExtrude","SWEPT_FACE",FACE,{"disambiguationData":[OSD([sQuery(id+"F6.wireOp",EDGE,"E37")])]}),makeQuery(id+"F7.opExtrude","SWEPT_FACE",FACE,{"disambiguationData":[OSD([sQuery(id+"F6.wireOp",EDGE,"E38")])]}),makeQuery(id+"F7.opExtrude","SWEPT_FACE",FACE,{"disambiguationData":[OSD([sQuery(id+"F6.wireOp",EDGE,"E39")])]}),makeQuery(id+"F7.opExtrude","SWEPT_FACE",FACE,{"disambiguationData":[OSD([sQuery(id+"F6.wireOp",EDGE,"E40"),sQuery(id+"F6.wireOp",EDGE,"E47")])]}),makeQuery(id+"F7.opExtrude","SWEPT_FACE",FACE,{"disambiguationData":[OSD([sQuery(id+"F6.wireOp",EDGE,"E41.MirrorCS"),sQuery(id+"F6.wireOp",EDGE,"E48")])]}),makeQuery(id+"F7.opExtrude","SWEPT_FACE",FACE,{"disambiguationData":[OSD([sQuery(id+"F6.wireOp",EDGE,"E42.MirrorCS")])]}),makeQuery(id+"F7.opExtrude","SWEPT_FACE",FACE,{"disambiguationData":[OSD([sQuery(id+"F6.wireOp",EDGE,"E43.MirrorCS")])]}),makeQuery(id+"F7.opExtrude","SWEPT_FACE",FACE,{"disambiguationData":[OSD([sQuery(id+"F6.wireOp",EDGE,"E44.MirrorCS")])]}),makeQuery(id+"F7.opExtrude","SWEPT_FACE",FACE,{"disambiguationData":[OSD([sQuery(id+"F6.wireOp",EDGE,"E45.MirrorCS")])]}),makeQuery(id+"F7.opExtrude","SWEPT_FACE",FACE,{"disambiguationData":[OSD([sQuery(id+"F6.wireOp",EDGE,"E46")])]}),makeQuery(id+"F7.opExtrude","SWEPT_FACE",FACE,{"disambiguationData":[OSD([sQuery(id+"F6.wireOp",EDGE,"020a8742-f3d3-43aa-8d11-e984b5552f450.MirrorCS")])]}),makeQuery(id+"F7.opExtrude","SWEPT_FACE",FACE,{"disambiguationData":[OSD([sQuery(id+"F6.wireOp",EDGE,"7f19501d-313e-40a1-b078-9e00cbc5491b")])]})])],"derivedFrom":subQ10});}
            var sketch = newSketch(context, id + "F12", { "sketchPlane" : qUnion([Q0])});
            skFitSpline(sketch, "E59", {"points": [v(-13.58, -38.64) * mm, v(-9.62, -37.76) * mm, v(0, -38.99) * mm, v(7.86, -37.85) * mm, v(13.48, -38.37) * mm, v(6.72, -42.06) * mm, v(0, -43.3) * mm, v(-7.17, -42.33) * mm, v(-13.58, -38.64) * mm]});
            skSolve(sketch);
        }
        {
            var Q0;
            Q0 = qSketchRegion(id + "F12", true);
            extrude(context, id + "F13", {"entities" : qUnion([Q0]), "operationType" : NewBodyOperationType.ADD, "depth" : 1 * mm, "offsetDistance" : 25.4 * mm});
        }
    });
